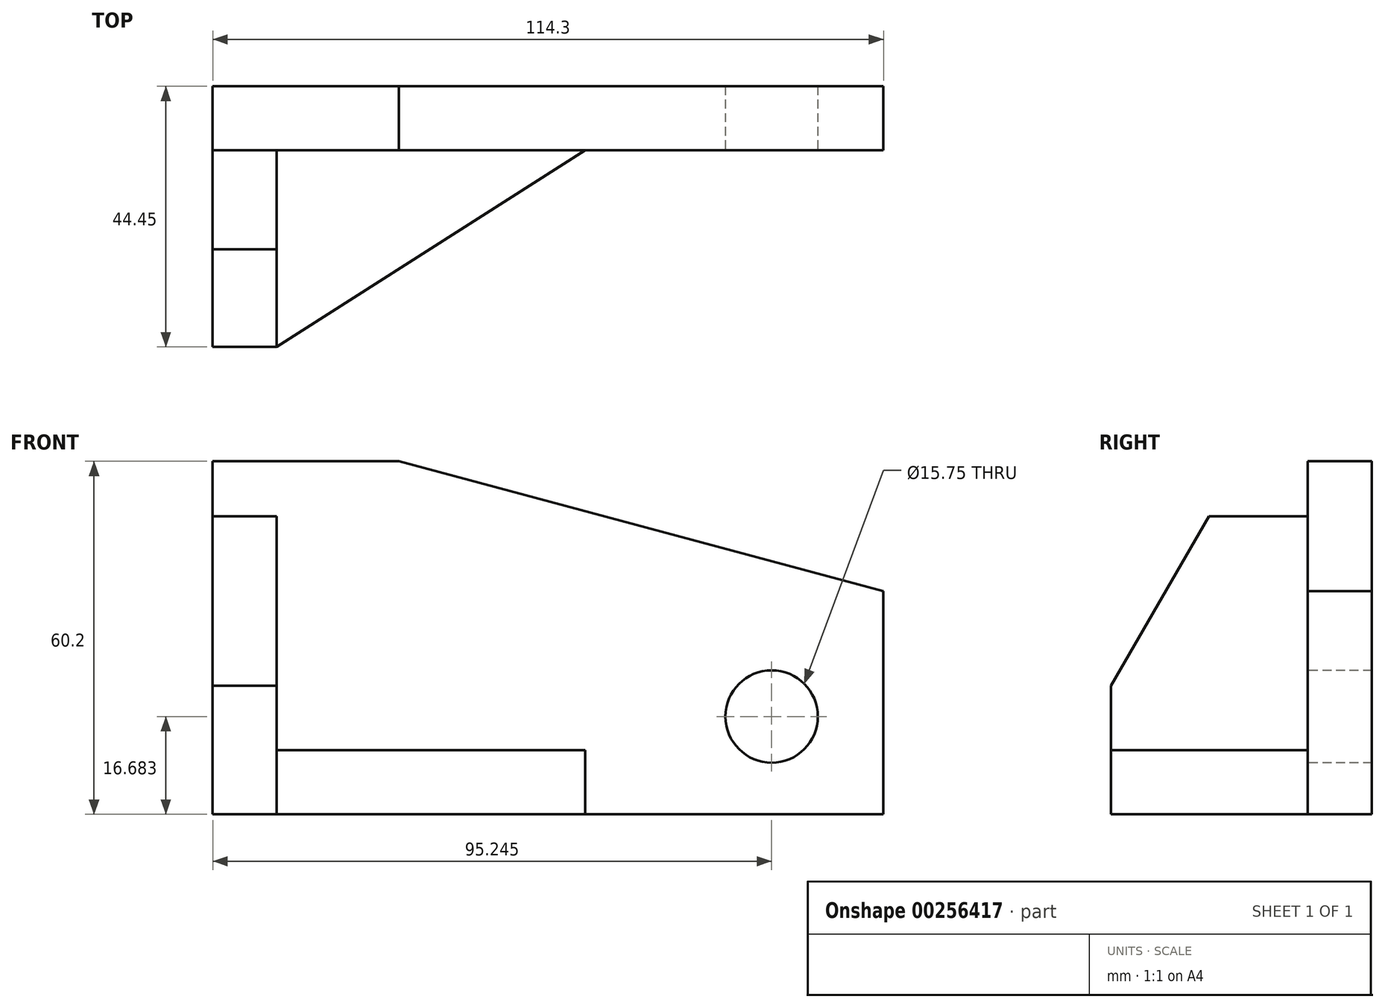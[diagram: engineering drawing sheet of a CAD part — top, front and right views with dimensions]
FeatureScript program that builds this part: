
annotation { "Feature Type Name" : "Feature", "Feature Type Description" : "" }
export const myFeature = defineFeature(function(context is Context, id is Id, definition is map)
    precondition{}
    {
        {
            var Q0;
            Q0=qCreatedBy(makeId("Front.planeOp"),FACE);
            var sketch = newSketch(context, id + "F0", { "sketchPlane" : qUnion([Q0])});
            skLineSegment(sketch, "E0", {"start": v(-77.93, -21.93) * mm, "end": v(36.37, -21.93) * mm});
            skLineSegment(sketch, "E1", {"start": v(-77.93, -21.93) * mm, "end": v(-77.93, 38.27) * mm});
            skLineSegment(sketch, "E2", {"start": v(-77.93, 38.27) * mm, "end": v(36.37, 38.27) * mm});
            skLineSegment(sketch, "E3", {"start": v(36.37, 38.27) * mm, "end": v(36.37, -21.93) * mm});
            skSolve(sketch);
        }
        {
            var Q0;
            Q0 = qSketchRegion(id + "F0", true);
            extrude(context, id + "F1", {"entities" : qUnion([Q0]), "depth" : 10.92 * mm});
        }
        {
            var Q0;
            Q0=makeQuery(id+"F1.opExtrude","CAP_FACE",FACE,{"disambiguationData":[OSD([sQuery(id+"F0.wireOp",EDGE,"E0"),sQuery(id+"F0.wireOp",EDGE,"E1"),sQuery(id+"F0.wireOp",EDGE,"E2"),sQuery(id+"F0.wireOp",EDGE,"E3")])],"isStart":false});
            var sketch = newSketch(context, id + "F2", { "sketchPlane" : qUnion([Q0])});
            skLineSegment(sketch, "E4", {"start": v(36.37, 16.15) * mm, "end": v(36.37, 38.27) * mm});
            skLineSegment(sketch, "E5", {"start": v(36.37, 38.27) * mm, "end": v(-46.18, 38.27) * mm});
            skLineSegment(sketch, "E6", {"start": v(-77.93, -21.93) * mm, "end": v(-14.43, -21.93) * mm});
            skLineSegment(sketch, "E7", {"start": v(-77.93, -21.93) * mm, "end": v(-77.93, 28.87) * mm});
            skLineSegment(sketch, "E8", {"start": v(-77.93, 28.87) * mm, "end": v(-14.43, 28.87) * mm});
            skLineSegment(sketch, "E9", {"start": v(-14.43, 28.87) * mm, "end": v(-14.43, -21.93) * mm});
            skSolve(sketch);
        }
        {
            var Q0;
            Q0 = qSketchRegion(id + "F2", true);
            extrude(context, id + "F3", {"entities" : qUnion([Q0]), "operationType" : NewBodyOperationType.ADD, "depth" : 33.53 * mm});
        }
        {
            var Q0;
            Q0=makeQuery(id+"F3.opExtrude","SWEPT_FACE",FACE,{"disambiguationData":[OSD([sQuery(id+"F2.wireOp",EDGE,"E8")])]});
            var sketch = newSketch(context, id + "F4", { "sketchPlane" : qUnion([Q0])});
            skLineSegment(sketch, "E10", {"start": v(-77.93, -44.45) * mm, "end": v(-67.01, -44.45) * mm});
            skLineSegment(sketch, "E11", {"start": v(-67.01, -44.45) * mm, "end": v(-67.01, -10.92) * mm});
            skLineSegment(sketch, "E12", {"start": v(-67.01, -10.92) * mm, "end": v(-77.93, -10.92) * mm});
            skLineSegment(sketch, "E13", {"start": v(-77.93, -10.92) * mm, "end": v(-77.93, -44.45) * mm});
            skLineSegment(sketch, "E14", {"start": v(-67.01, -44.45) * mm, "end": v(-14.43, -10.92) * mm});
            skLineSegment(sketch, "E15", {"start": v(-14.43, -10.92) * mm, "end": v(-67.01, -10.92) * mm});
            skSolve(sketch);
        }
        {
            var Q0;
            {var subQ0=sQuery(id+"F4.wireOp",EDGE,"E14");Q0=makeQuery(id+"F4.imprint","IMPRINT",FACE,{"disambiguationData":[TD([[makeQuery(id+"F4.imprint","IMPRINT",EDGE,{"derivedFrom":subQ0}),-1.0]])]});}
            extrude(context, id + "F5", {"entities" : qUnion([Q0]), "operationType" : NewBodyOperationType.REMOVE, "oppositeDirection" : true, "depth" : 50.8 * mm});
        }
        {
            var Q0;
            Q0=makeQuery(id+"F7.boolean.opBoolean","MERGE",FACE,{"derivedFrom":[makeQuery(id+"F1.opExtrude","CAP_FACE",FACE,{"disambiguationData":[OSD([sQuery(id+"F0.wireOp",EDGE,"E0"),sQuery(id+"F0.wireOp",EDGE,"E1"),sQuery(id+"F0.wireOp",EDGE,"E2"),sQuery(id+"F0.wireOp",EDGE,"E3")])],"isStart":false}),makeQuery(id+"F7.opExtrude","SWEPT_FACE",FACE,{"disambiguationData":[OSD([sQuery(id+"F4.wireOp",EDGE,"E15")])]})]});
            var sketch = newSketch(context, id + "F6", { "sketchPlane" : qUnion([Q0])});
            skCircle(sketch, "E16", {"center": v(17.32, -5.25) * mm, "radius": 7.87 * mm});
            skPoint(sketch, "E17.endSnap0", {"position": v(-40.72, -11) * mm});
            skSolve(sketch);
        }
        {
            var Q0;
            Q0=makeQuery(id+"F4.imprint","IMPRINT",FACE,{"disambiguationData":[TD([[makeQuery(id+"F4.imprint","IMPRINT",EDGE,{"derivedFrom":sQuery(id+"F4.wireOp",EDGE,"E11")}),-1.0]])]});
            extrude(context, id + "F7", {"entities" : qUnion([Q0]), "operationType" : NewBodyOperationType.REMOVE, "oppositeDirection" : true, "depth" : 39.88 * mm});
        }
        {
            var Q0;
            Q0 = qSketchRegion(id + "F6", true);
            extrude(context, id + "F8", {"entities" : qUnion([Q0]), "operationType" : NewBodyOperationType.REMOVE, "oppositeDirection" : true, "depth" : 10.92 * mm});
        }
        {
            var Q0;
            Q0=makeQuery(id+"F7.boolean.opBoolean","MERGE",FACE,{"derivedFrom":[makeQuery(id+"F1.opExtrude","CAP_FACE",FACE,{"disambiguationData":[OSD([sQuery(id+"F0.wireOp",EDGE,"E0"),sQuery(id+"F0.wireOp",EDGE,"E1"),sQuery(id+"F0.wireOp",EDGE,"E2"),sQuery(id+"F0.wireOp",EDGE,"E3")])],"isStart":false}),makeQuery(id+"F7.opExtrude","SWEPT_FACE",FACE,{"disambiguationData":[OSD([sQuery(id+"F4.wireOp",EDGE,"E15")])]})]});
            var sketch = newSketch(context, id + "F9", { "sketchPlane" : qUnion([Q0])});
            skLineSegment(sketch, "E18", {"start": v(-77.93, 38.27) * mm, "end": v(-46.18, 38.27) * mm});
            skLineSegment(sketch, "E19", {"start": v(-46.18, 38.27) * mm, "end": v(36.37, 38.27) * mm});
            skLineSegment(sketch, "E20", {"start": v(36.37, 38.27) * mm, "end": v(36.37, 16.15) * mm});
            skLineSegment(sketch, "E21", {"start": v(36.37, 16.15) * mm, "end": v(-46.18, 38.27) * mm});
            skSolve(sketch);
        }
        {
            var Q0;
            Q0 = qSketchRegion(id + "F9", true);
            extrude(context, id + "F10", {"entities" : qUnion([Q0]), "operationType" : NewBodyOperationType.REMOVE, "oppositeDirection" : true, "depth" : 11.94 * mm});
        }
        {
            var Q0;
            Q0=makeQuery(id+"F3.boolean.opBoolean","MERGE",FACE,{"derivedFrom":[makeQuery(id+"F1.opExtrude","SWEPT_FACE",FACE,{"disambiguationData":[OSD([sQuery(id+"F0.wireOp",EDGE,"E1")])]}),makeQuery(id+"F3.opExtrude","SWEPT_FACE",FACE,{"disambiguationData":[OSD([sQuery(id+"F2.wireOp",EDGE,"E7")])]})]});
            var sketch = newSketch(context, id + "F11", { "sketchPlane" : qUnion([Q0])});
            skLineSegment(sketch, "E22", {"start": v(44.45, -21.93) * mm, "end": v(44.45, 0) * mm});
            skLineSegment(sketch, "E23", {"start": v(44.45, 0) * mm, "end": v(44.45, 28.87) * mm});
            skLineSegment(sketch, "E24", {"start": v(44.45, 28.87) * mm, "end": v(27.78, 28.87) * mm});
            skLineSegment(sketch, "E25", {"start": v(27.78, 28.87) * mm, "end": v(44.45, 0) * mm});
            skSolve(sketch);
        }
        {
            var Q0;
            Q0 = qSketchRegion(id + "F11", true);
            extrude(context, id + "F12", {"entities" : qUnion([Q0]), "operationType" : NewBodyOperationType.REMOVE, "oppositeDirection" : true, "depth" : 10.92 * mm});
        }
    });
